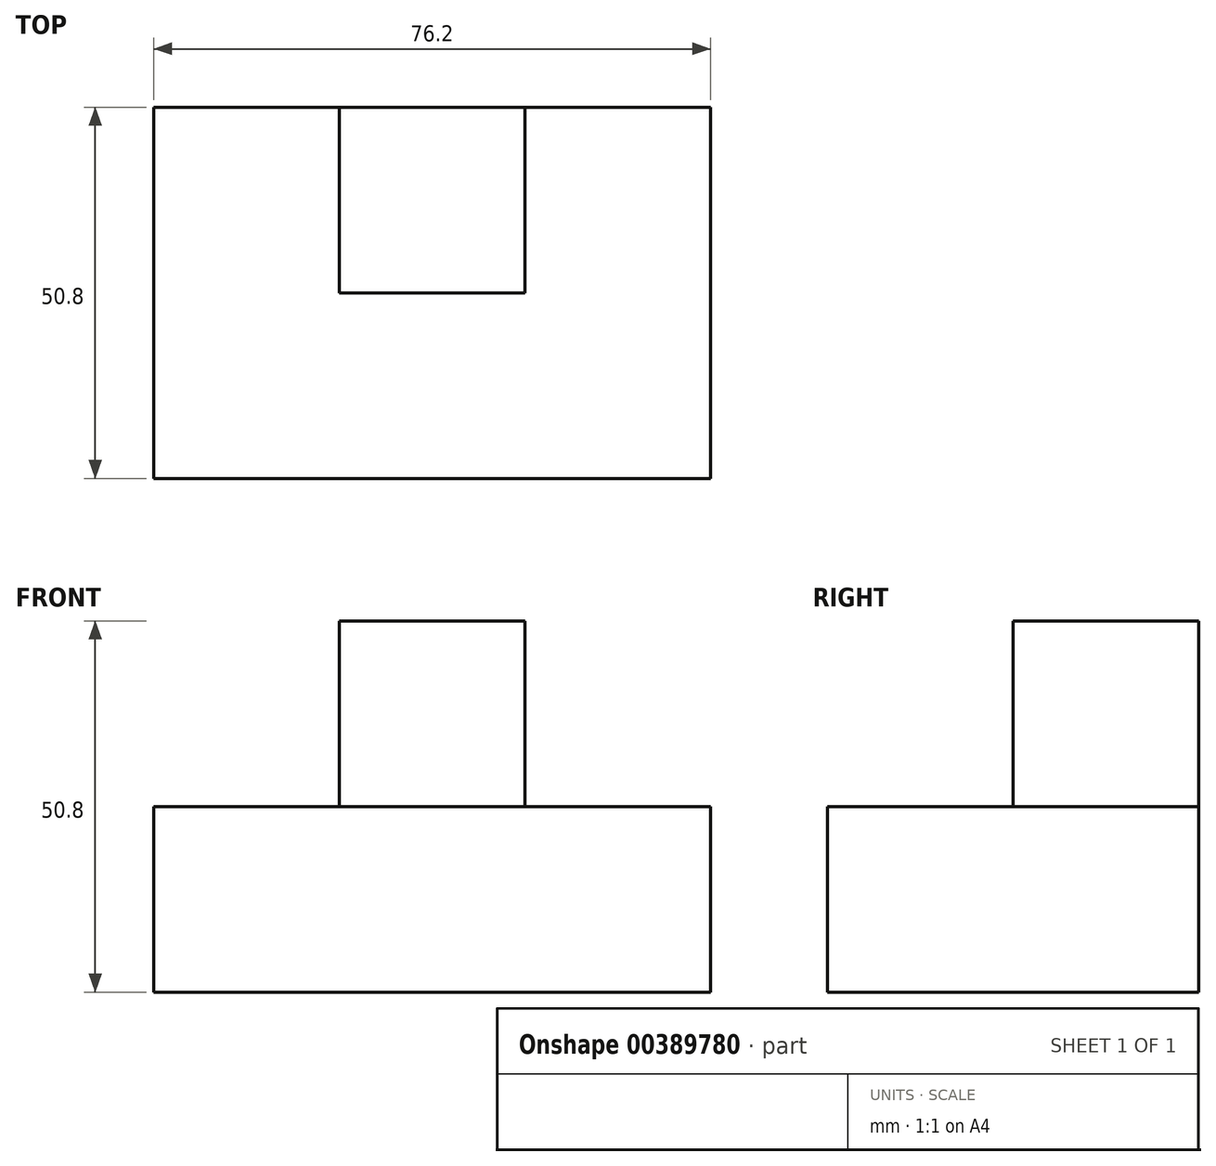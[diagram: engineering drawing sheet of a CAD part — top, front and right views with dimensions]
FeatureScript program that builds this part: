
annotation { "Feature Type Name" : "Feature", "Feature Type Description" : "" }
export const myFeature = defineFeature(function(context is Context, id is Id, definition is map)
    precondition{}
    {
        {
            var Q0;
            Q0=qCreatedBy(makeId("Front.planeOp"),FACE);
            var sketch = newSketch(context, id + "F0", { "sketchPlane" : qUnion([Q0])});
            skLineSegment(sketch, "E0.bottom", {"start": v(0, 0) * mm, "end": v(-25.4, 0) * mm});
            skLineSegment(sketch, "E0.top", {"start": v(0, 25.4) * mm, "end": v(-25.4, 25.4) * mm});
            skLineSegment(sketch, "E0.left", {"start": v(0, 0) * mm, "end": v(0, 25.4) * mm});
            skLineSegment(sketch, "E0.right", {"start": v(-25.4, 0) * mm, "end": v(-25.4, 25.4) * mm});
            skLineSegment(sketch, "E1.bottom", {"start": v(0, 0) * mm, "end": v(25.4, 0) * mm});
            skLineSegment(sketch, "E1.top", {"start": v(0, 25.4) * mm, "end": v(25.4, 25.4) * mm});
            skLineSegment(sketch, "E1.right", {"start": v(25.4, 0) * mm, "end": v(25.4, 25.4) * mm});
            skLineSegment(sketch, "E2.bottom", {"start": v(25.4, 25.4) * mm, "end": v(50.8, 25.4) * mm});
            skLineSegment(sketch, "E2.top", {"start": v(25.4, 0) * mm, "end": v(50.8, 0) * mm});
            skLineSegment(sketch, "E2.left", {"start": v(25.4, 25.4) * mm, "end": v(25.4, 0) * mm});
            skLineSegment(sketch, "E2.right", {"start": v(50.8, 25.4) * mm, "end": v(50.8, 0) * mm});
            skLineSegment(sketch, "E3.top", {"start": v(0, 50.8) * mm, "end": v(25.4, 50.8) * mm});
            skLineSegment(sketch, "E3.left", {"start": v(0, 25.4) * mm, "end": v(0, 50.8) * mm});
            skLineSegment(sketch, "E3.right", {"start": v(25.4, 25.4) * mm, "end": v(25.4, 50.8) * mm});
            skSolve(sketch);
        }
        {
            var Q0;
            Q0=makeQuery(id+"F0.imprint","IMPRINT",FACE,{"disambiguationData":[TD([[makeQuery(id+"F0.imprint","IMPRINT",EDGE,{"derivedFrom":sQuery(id+"F0.wireOp",EDGE,"E0.bottom")}),-1.0]])]});
            var sketch = newSketch(context, id + "F1", { "sketchPlane" : qUnion([Q0])});
            skSolve(sketch);
        }
        {
            var Q0;
            Q0 = qSketchRegion(id + "F1", true);
            var Q1;
            Q1=makeQuery(id+"F0.imprint","IMPRINT",FACE,{"disambiguationData":[TD([[makeQuery(id+"F0.imprint","IMPRINT",EDGE,{"derivedFrom":sQuery(id+"F0.wireOp",EDGE,"E0.bottom")}),-1.0]])]});
            var Q2;
            Q2=makeQuery(id+"F0.imprint","IMPRINT",FACE,{"disambiguationData":[TD([[makeQuery(id+"F0.imprint","IMPRINT",EDGE,{"derivedFrom":sQuery(id+"F0.wireOp",EDGE,"E1.top")}),1.0]])]});
            var Q3;
            Q3=makeQuery(id+"F0.imprint","IMPRINT",FACE,{"disambiguationData":[TD([[makeQuery(id+"F0.imprint","IMPRINT",EDGE,{"derivedFrom":sQuery(id+"F0.wireOp",EDGE,"E1.bottom")}),1.0]])]});
            var Q4;
            Q4=makeQuery(id+"F0.imprint","IMPRINT",FACE,{"disambiguationData":[TD([[makeQuery(id+"F0.imprint","IMPRINT",EDGE,{"derivedFrom":sQuery(id+"F0.wireOp",EDGE,"E2.bottom")}),-1.0]])]});
            extrude(context, id + "F2", {"entities" : qUnion([Q0, Q1, Q2, Q3, Q4]), "depth" : 25.4 * mm});
        }
        {
            var Q0;
            Q0=qCreatedBy(makeId("Front.planeOp"),FACE);
            var sketch = newSketch(context, id + "F3", { "sketchPlane" : qUnion([Q0])});
            skLineSegment(sketch, "E4.bottom", {"start": v(0, 0) * mm, "end": v(-25.4, 0) * mm});
            skLineSegment(sketch, "E4.top", {"start": v(0, 25.4) * mm, "end": v(-25.4, 25.4) * mm});
            skLineSegment(sketch, "E4.left", {"start": v(0, 0) * mm, "end": v(0, 25.4) * mm});
            skLineSegment(sketch, "E4.right", {"start": v(-25.4, 0) * mm, "end": v(-25.4, 25.4) * mm});
            skLineSegment(sketch, "E5.bottom", {"start": v(50.8, 0) * mm, "end": v(25.4, 0) * mm});
            skLineSegment(sketch, "E5.top", {"start": v(50.8, 25.4) * mm, "end": v(25.4, 25.4) * mm});
            skLineSegment(sketch, "E5.left", {"start": v(50.8, 0) * mm, "end": v(50.8, 25.4) * mm});
            skLineSegment(sketch, "E5.right", {"start": v(25.4, 0) * mm, "end": v(25.4, 25.4) * mm});
            skLineSegment(sketch, "E6.bottom", {"start": v(25.4, 0) * mm, "end": v(0, 0) * mm});
            skLineSegment(sketch, "E6.top", {"start": v(25.4, 25.4) * mm, "end": v(0, 25.4) * mm});
            skSolve(sketch);
        }
        {
            var Q0;
            Q0=makeQuery(id+"F3.imprint","IMPRINT",FACE,{"disambiguationData":[TD([[makeQuery(id+"F3.imprint","IMPRINT",EDGE,{"derivedFrom":sQuery(id+"F3.wireOp",EDGE,"E4.bottom")}),-1.0]])]});
            var Q1;
            Q1=makeQuery(id+"F1.imprint","IMPRINT",FACE,{"disambiguationData":[TD([[makeQuery(id+"F1.imprint","IMPRINT",EDGE,{"derivedFrom":makeQuery(id+"F0.imprint","IMPRINT",EDGE,{"derivedFrom":sQuery(id+"F0.wireOp",EDGE,"E0.bottom")})}),-1.0]])]});
            extrude(context, id + "F4", {"entities" : qUnion([Q0, Q1]), "operationType" : NewBodyOperationType.ADD, "depth" : 25.4 * mm});
        }
        {
            var Q0;
            Q0=qCreatedBy(makeId("Front.planeOp"),FACE);
            var sketch = newSketch(context, id + "F5", { "sketchPlane" : qUnion([Q0])});
            skLineSegment(sketch, "E7.bottom", {"start": v(0, 0) * mm, "end": v(-25.4, 0) * mm});
            skLineSegment(sketch, "E7.top", {"start": v(0, 25.4) * mm, "end": v(-25.4, 25.4) * mm});
            skLineSegment(sketch, "E7.left", {"start": v(0, 0) * mm, "end": v(0, 25.4) * mm});
            skLineSegment(sketch, "E7.right", {"start": v(-25.4, 0) * mm, "end": v(-25.4, 25.4) * mm});
            skLineSegment(sketch, "E8.bottom", {"start": v(0, 25.4) * mm, "end": v(25.4, 25.4) * mm});
            skLineSegment(sketch, "E8.top", {"start": v(0, 0) * mm, "end": v(25.4, 0) * mm});
            skLineSegment(sketch, "E8.left", {"start": v(0, 25.4) * mm, "end": v(0, 0) * mm});
            skLineSegment(sketch, "E8.right", {"start": v(25.4, 25.4) * mm, "end": v(25.4, 0) * mm});
            skLineSegment(sketch, "E9.bottom", {"start": v(25.4, 25.4) * mm, "end": v(50.8, 25.4) * mm});
            skLineSegment(sketch, "E9.top", {"start": v(25.4, 0) * mm, "end": v(50.8, 0) * mm});
            skLineSegment(sketch, "E9.right", {"start": v(50.8, 25.4) * mm, "end": v(50.8, 0) * mm});
            skSolve(sketch);
        }
        {
            var Q0;
            Q0=makeQuery(id+"F5.imprint","IMPRINT",FACE,{"disambiguationData":[TD([[makeQuery(id+"F5.imprint","IMPRINT",EDGE,{"derivedFrom":sQuery(id+"F5.wireOp",EDGE,"E8.bottom")}),-1.0]])]});
            var Q1;
            Q1=makeQuery(id+"F5.imprint","IMPRINT",FACE,{"disambiguationData":[TD([[makeQuery(id+"F5.imprint","IMPRINT",EDGE,{"derivedFrom":sQuery(id+"F5.wireOp",EDGE,"E9.bottom")}),-1.0]])]});
            var Q2;
            Q2=makeQuery(id+"F5.imprint","IMPRINT",FACE,{"disambiguationData":[TD([[makeQuery(id+"F5.imprint","IMPRINT",EDGE,{"derivedFrom":sQuery(id+"F5.wireOp",EDGE,"E7.bottom")}),-1.0]])]});
            extrude(context, id + "F6", {"entities" : qUnion([Q0, Q1, Q2]), "operationType" : NewBodyOperationType.ADD, "depth" : 25.4 * mm});
        }
        {
            var Q0;
            Q0=makeQuery(id+"F2.opExtrude","CAP_FACE",FACE,{"disambiguationData":[OSD([sQuery(id+"F0.wireOp",EDGE,"E0.bottom"),sQuery(id+"F0.wireOp",EDGE,"E0.top"),sQuery(id+"F0.wireOp",EDGE,"E0.right"),sQuery(id+"F0.wireOp",EDGE,"E1.bottom"),sQuery(id+"F0.wireOp",EDGE,"E2.bottom"),sQuery(id+"F0.wireOp",EDGE,"E2.top"),sQuery(id+"F0.wireOp",EDGE,"E2.right"),sQuery(id+"F0.wireOp",EDGE,"E3.top"),sQuery(id+"F0.wireOp",EDGE,"E3.left"),sQuery(id+"F0.wireOp",EDGE,"E3.right")])],"isStart":false});
            var sketch = newSketch(context, id + "F7", { "sketchPlane" : qUnion([Q0])});
            skLineSegment(sketch, "E10.bottom", {"start": v(-25.4, 25.4) * mm, "end": v(0, 25.4) * mm});
            skLineSegment(sketch, "E10.top", {"start": v(-25.4, 0) * mm, "end": v(0, 0) * mm});
            skLineSegment(sketch, "E10.left", {"start": v(-25.4, 25.4) * mm, "end": v(-25.4, 0) * mm});
            skLineSegment(sketch, "E10.right", {"start": v(0, 25.4) * mm, "end": v(0, 0) * mm});
            skLineSegment(sketch, "E11.bottom", {"start": v(0, 25.4) * mm, "end": v(25.4, 25.4) * mm});
            skLineSegment(sketch, "E11.top", {"start": v(0, 0) * mm, "end": v(25.4, 0) * mm});
            skLineSegment(sketch, "E11.right", {"start": v(25.4, 25.4) * mm, "end": v(25.4, 0) * mm});
            skLineSegment(sketch, "E12.bottom", {"start": v(25.4, 25.4) * mm, "end": v(50.8, 25.4) * mm});
            skLineSegment(sketch, "E12.top", {"start": v(25.4, 0) * mm, "end": v(50.8, 0) * mm});
            skLineSegment(sketch, "E12.right", {"start": v(50.8, 25.4) * mm, "end": v(50.8, 0) * mm});
            skSolve(sketch);
        }
        {
            var Q0;
            Q0=makeQuery(id+"F7.imprint","IMPRINT",FACE,{"disambiguationData":[TD([[makeQuery(id+"F7.imprint","IMPRINT",EDGE,{"derivedFrom":sQuery(id+"F7.wireOp",EDGE,"E10.bottom")}),1.0]])]});
            var Q1;
            Q1=makeQuery(id+"F7.imprint","IMPRINT",FACE,{"disambiguationData":[TD([[makeQuery(id+"F7.imprint","IMPRINT",EDGE,{"derivedFrom":sQuery(id+"F7.wireOp",EDGE,"E11.bottom")}),-1.0]])]});
            var Q2;
            Q2=makeQuery(id+"F7.imprint","IMPRINT",FACE,{"disambiguationData":[TD([[makeQuery(id+"F7.imprint","IMPRINT",EDGE,{"derivedFrom":sQuery(id+"F7.wireOp",EDGE,"E12.bottom")}),-1.0]])]});
            extrude(context, id + "F8", {"entities" : qUnion([Q0, Q1, Q2]), "operationType" : NewBodyOperationType.ADD, "depth" : 25.4 * mm});
        }
    });
